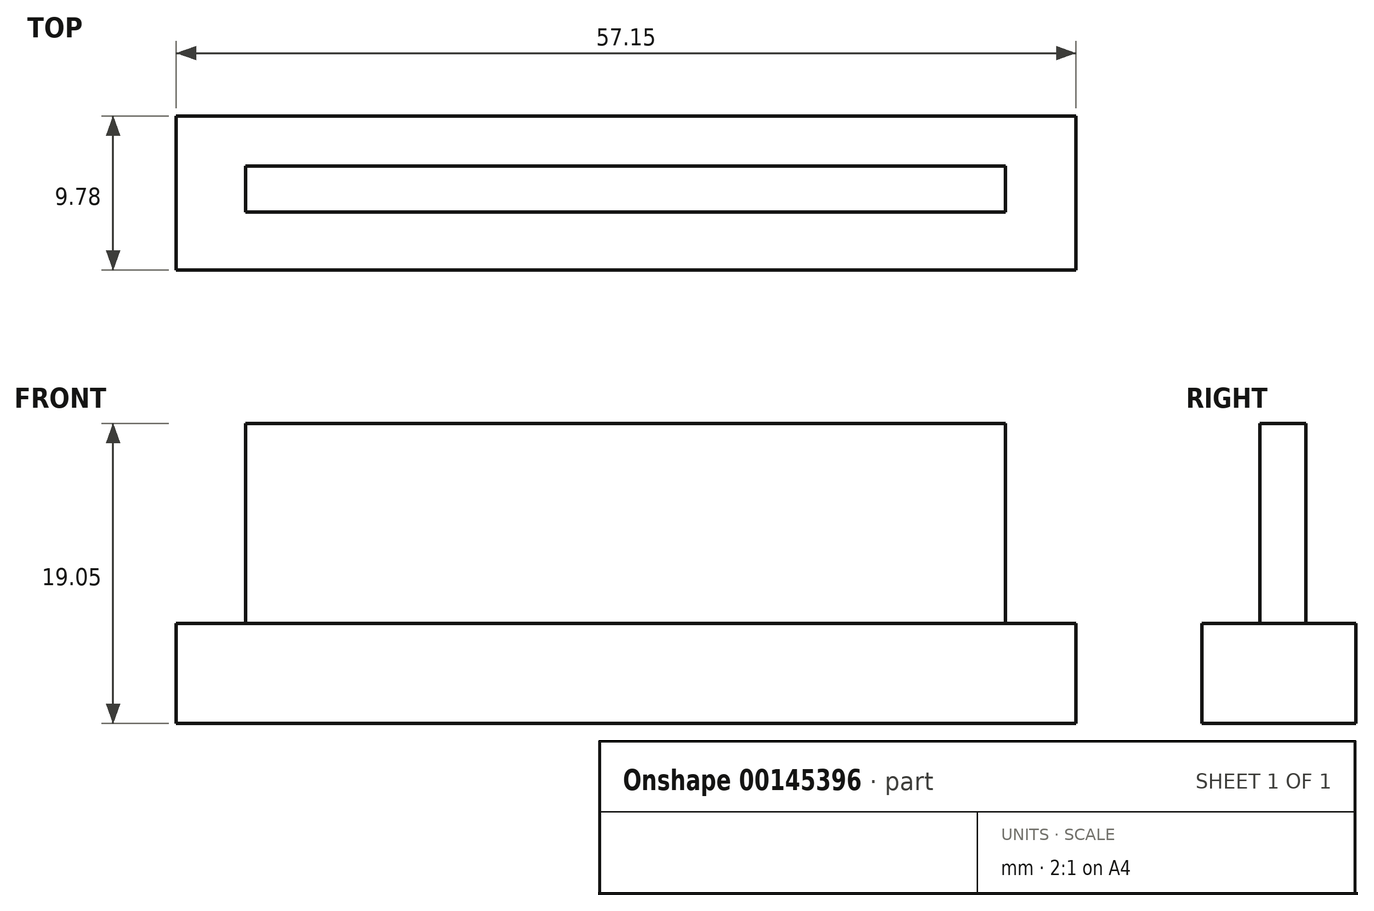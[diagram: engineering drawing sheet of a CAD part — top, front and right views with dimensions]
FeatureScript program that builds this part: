
annotation { "Feature Type Name" : "Feature", "Feature Type Description" : "" }
export const myFeature = defineFeature(function(context is Context, id is Id, definition is map)
    precondition{}
    {
        {
            var Q0;
            Q0=qCreatedBy(makeId("Top.planeOp"),FACE);
            var sketch = newSketch(context, id + "F0", { "sketchPlane" : qUnion([Q0])});
            skLineSegment(sketch, "E0.bottom", {"start": v(24.76, -0.26) * mm, "end": v(-23.5, -0.26) * mm});
            skLineSegment(sketch, "E0.top", {"start": v(24.76, 2.66) * mm, "end": v(-23.5, 2.66) * mm});
            skLineSegment(sketch, "E0.left", {"start": v(24.76, -0.26) * mm, "end": v(24.76, 2.66) * mm});
            skLineSegment(sketch, "E0.right", {"start": v(-23.5, -0.26) * mm, "end": v(-23.5, 2.66) * mm});
            skPoint(sketch, "E0.middle", {"position": v(0.63, 1.2) * mm});
            skLineSegment(sketch, "E1.0", {"start": v(29.26, 5.84) * mm, "end": v(-27.9, 5.84) * mm});
            skLineSegment(sketch, "E1.1", {"start": v(29.26, -3.94) * mm, "end": v(29.26, 5.84) * mm});
            skLineSegment(sketch, "E1.2", {"start": v(29.26, -3.94) * mm, "end": v(-27.9, -3.94) * mm});
            skLineSegment(sketch, "E1.3", {"start": v(-27.9, -3.94) * mm, "end": v(-27.9, 5.84) * mm});
            skSolve(sketch);
        }
        {
            var Q0;
            Q0=makeQuery(id+"F0.imprint","IMPRINT",FACE,{"disambiguationData":[TD([[makeQuery(id+"F0.imprint","IMPRINT",EDGE,{"derivedFrom":sQuery(id+"F0.wireOp",EDGE,"E0.bottom")}),1.0]])]});
            extrude(context, id + "F1", {"entities" : qUnion([Q0]), "depth" : 6.35 * mm});
        }
        {
            var Q0;
            Q0=makeQuery(id+"F0.imprint","IMPRINT",FACE,{"disambiguationData":[TD([[makeQuery(id+"F0.imprint","IMPRINT",EDGE,{"derivedFrom":sQuery(id+"F0.wireOp",EDGE,"E0.bottom")}),-1.0]])]});
            extrude(context, id + "F2", {"entities" : qUnion([Q0]), "operationType" : NewBodyOperationType.ADD, "depth" : 19.05 * mm});
        }
    });
